# Revit family: Power-ModularDevices-GEWISS-90MCB-MT100_2P
name_source: partatom
category: Apparecchi elettrici
revit_build: Autodesk Revit MEP 2016 (Build: 20150220_1215(x64)
units: mm (PartAtom-declared; Revit-internal decimal feet)

## family parameters
Condiviso = Sì
Host = Superficie
Mantenere orientamento annotazione = Sì
Numero OmniClass = 23.80.30.14
Punto di calcolo locali = Sì
Quota connettore circolare = Usa diametro
Taglio con vuoti quando caricato = No
Tipo di parte = Normale
Titolo OmniClass = Power Distribution

## types (1)
- Power-ModularDevices-GEWISS-90MCB-MT100_2P
    Altezza = 85 mm  [stored 0.278871 ft]
    Breaking capacity (EN 60898) = 10000A
    Breaking capacity EN 60898 (Ics) = 0.75 x Icn
    Breaking capacity EN 60898 230V (Icn) = 10000A
    Breaking capacity EN 60898 400V (Icn) = 10000A
    Breaking capacity EN 60947-2 (Ics) = 50% Icu
    Breaking capacity EN 60947-2 230V (Icu) = 30KA
    Breaking capacity EN 60947-2 400V (Icu) = 20KA
    Breaking capacity EN 61009-1 (Ics) = 1 x Icn
    Carico apparente = 0 VA
    Catalogue = POWER
    Catalogue Range = 90 MCB
    Curve = D
    Description = MINIATURE CIRCUIT BREAKER
    Descrizione = MCB 2P D13 10KA 2M
    EAN code = 8011564225510
    Electrical endurance = 10000
    Electrocod = 1411
    Finitura = GW - grigio chiaro
    IDF = 1192901e-7424-4489-baad-3a66a9d0fe16
    IDT = 31c722a8-5080-4331-a803-fcf7328b02f0
    Immagine tipo = GW94006.jpg
    Insulation voltage = 500V
    Interuttore = GW - grigio scuro
    Label = MT 100
    Larghezza = 36 mm  [stored 0.11811 ft]
    Level of immunity (8/20 µs) = 250A
    Maximum operating voltage = 440V AC / 220V DC
    Mechanical endurance = 20.000
    Minimum operating voltage = 12V ac/dc
    Modello = GW92754
    No. modules = 2
    No. of modules EN 50022 = 2
    No. of poles = 2P
    Number of poles = 2P
    Numero di poli_ = 2
    Operating temperature = -25 +60 °C
    Parti incassate = Sì
    Precision = 30 mA
    Produttore = GEWISS S.p.A.
    Prospetto di default = 1219 mm
    Rated current (In) = 13A
    Rated current: = 13A
    Rated frequency (Hz) = 50/60 Hz
    Rated impulse withstand voltage = 4KV
    Rated insulation voltage (Ui) = 500V
    Rated residual operating current = 30MA
    Rated tightening torque = 2 Nm
    Rated voltage = 230-400V
    SEO = MCB
    Section flexible cable = <=1x35 - <=2x16 - <=1x16+2x10 mm²
    Section rigid cable = <=1x35 - <=2x16 - <=1x16+2x10 mm²
    Spessore = 150 mm
    Standard = EN 60898, EN 60947-2
    Standard; = EN 60898, EN 60947-2
    Stocking temperature = -40 +70 °C
    Technical sheet = https://www.gewiss.com
    Type = AC
    URL = https://www.gewiss.com
    Version file RFA = 19.0
    Voltaggio = 230 V

note: [stored X ft] marks values corroborated as IEEE doubles in the binary element streams (Revit-internal decimal feet)

## geometry (parser evidence)
native form markers: Sweep x2
no freeform markers — native parametric forms only
